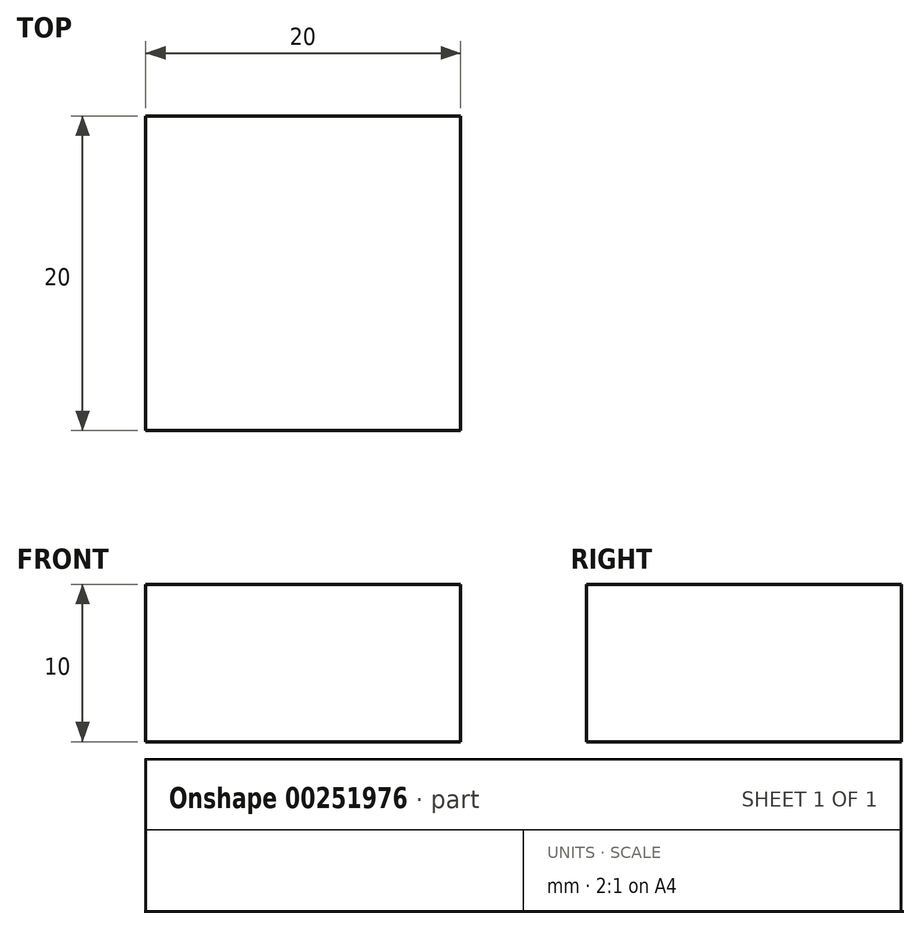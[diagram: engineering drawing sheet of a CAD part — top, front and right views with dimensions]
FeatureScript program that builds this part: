
annotation { "Feature Type Name" : "Feature", "Feature Type Description" : "" }
export const myFeature = defineFeature(function(context is Context, id is Id, definition is map)
    precondition{}
    {
        {
            var Q0;
            Q0=qCreatedBy(makeId("Front.planeOp"),FACE);
            var sketch = newSketch(context, id + "F0", { "sketchPlane" : qUnion([Q0])});
            skLineSegment(sketch, "E0.bottom", {"start": v(0, 0) * mm, "end": v(20, 0) * mm});
            skLineSegment(sketch, "E0.top", {"start": v(0, 10) * mm, "end": v(20, 10) * mm});
            skLineSegment(sketch, "E0.left", {"start": v(0, 0) * mm, "end": v(0, 10) * mm});
            skLineSegment(sketch, "E0.right", {"start": v(20, 0) * mm, "end": v(20, 10) * mm});
            skSolve(sketch);
        }
        {
            var Q0;
            Q0=makeQuery(id+"F0.imprint","IMPRINT",FACE,{"disambiguationData":[TD([[makeQuery(id+"F0.imprint","IMPRINT",EDGE,{"derivedFrom":sQuery(id+"F0.wireOp",EDGE,"E0.bottom")}),1.0]])]});
            extrude(context, id + "F1", {"entities" : qUnion([Q0]), "depth" : 20 * mm});
        }
    });
